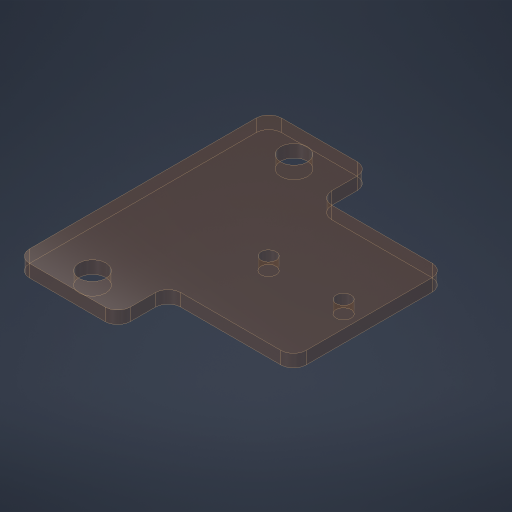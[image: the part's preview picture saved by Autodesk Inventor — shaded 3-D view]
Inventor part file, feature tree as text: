
AUTODESK INVENTOR PART (.ipt)
format: ipt  version: 2023.4 (Build 274418000, 418)  size: 217,600 bytes
history: native  units: in
note: dims shown in document units (in); Inventor stores cm internally (conversion verified against a paired STEP export)
features: sketch x3, hole x2, extrude x1, fillet x1
ambient origin geometry x8: Origin, YZ Plane, XZ Plane, XY Plane, X Axis, Y Axis, Z Axis, Center Point
bodies: Solid1 (feature_tree)
feature tree (7):
  extrude  "Extrusion1"  Depth=2.5in
  hole  "Hole1"  [1 undecoded]
  hole  "Hole2"  [1 undecoded]
  fillet  "Fillet1"  Radius=1.245in
  sketch  "Sketch1"  dims[d0=1.0in d1=2.5in]
  sketch  "Sketch2"  dims[d2=0.125in d3=0.0in d4=2.0in]
  sketch  "Sketch3"  dims[d6=0.266in d7=0.432in d8=0.119in d9=0.25in d10=0.5635in d11=1.0in d12=0.8108in d13=0.7447in d14=0.15in d15=0.75in d16=0.279in d17=0.25in d18=0.5635in d19=1.0in d20=0.8108in d21=1.245in d22=0.5in d23=0.5in d24=0.253in d25=0.125in]
note: 2 required parameter values undecoded (feature->parameter linkage not recoverable at this tier; creation-order binding heuristic only, values carry confidence <= 0.55)
